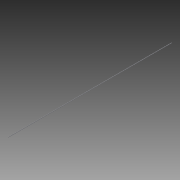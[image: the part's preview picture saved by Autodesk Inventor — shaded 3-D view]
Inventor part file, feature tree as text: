
AUTODESK INVENTOR PART (.ipt)
format: ipt  version: 2015 SP1 (Build 190203100, 203)  size: 64,000 bytes
history: native  units: in
note: dims shown in document units (in); Inventor stores cm internally (conversion verified against a paired STEP export)
features: extrude x1, sketch x1
ambient origin geometry x8: Origin, YZ Plane, XZ Plane, XY Plane, X Axis, Y Axis, Z Axis, Center Point
bodies: Solid1 (feature_tree)
feature tree (2):
  extrude  "Extrusion1"  Depth=40.0in TaperAngle=0.0deg
  sketch  "Sketch1"  dims[d0=0.125in d1=40.0in d2=0.0in]
